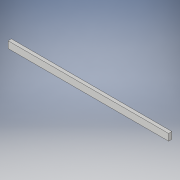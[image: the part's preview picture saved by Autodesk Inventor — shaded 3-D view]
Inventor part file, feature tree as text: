
AUTODESK INVENTOR PART (.ipt)
format: ipt  version: 2017 (Build 210142000, 142)  size: 91,136 bytes
history: native  units: in
note: dims shown in document units (in); Inventor stores cm internally (conversion verified against a paired STEP export)
features: extrude x1, sketch x1
ambient origin geometry x8: Origin, YZ Plane, XZ Plane, XY Plane, X Axis, Y Axis, Z Axis, Center Point
bodies: Solid1 (feature_tree)
feature tree (2):
  extrude  "Extrusion1"  Depth=3.0in
  sketch  "Sketch1"  dims[d0=72.0in d1=3.0in d2=1.5in d3=0.0in]
